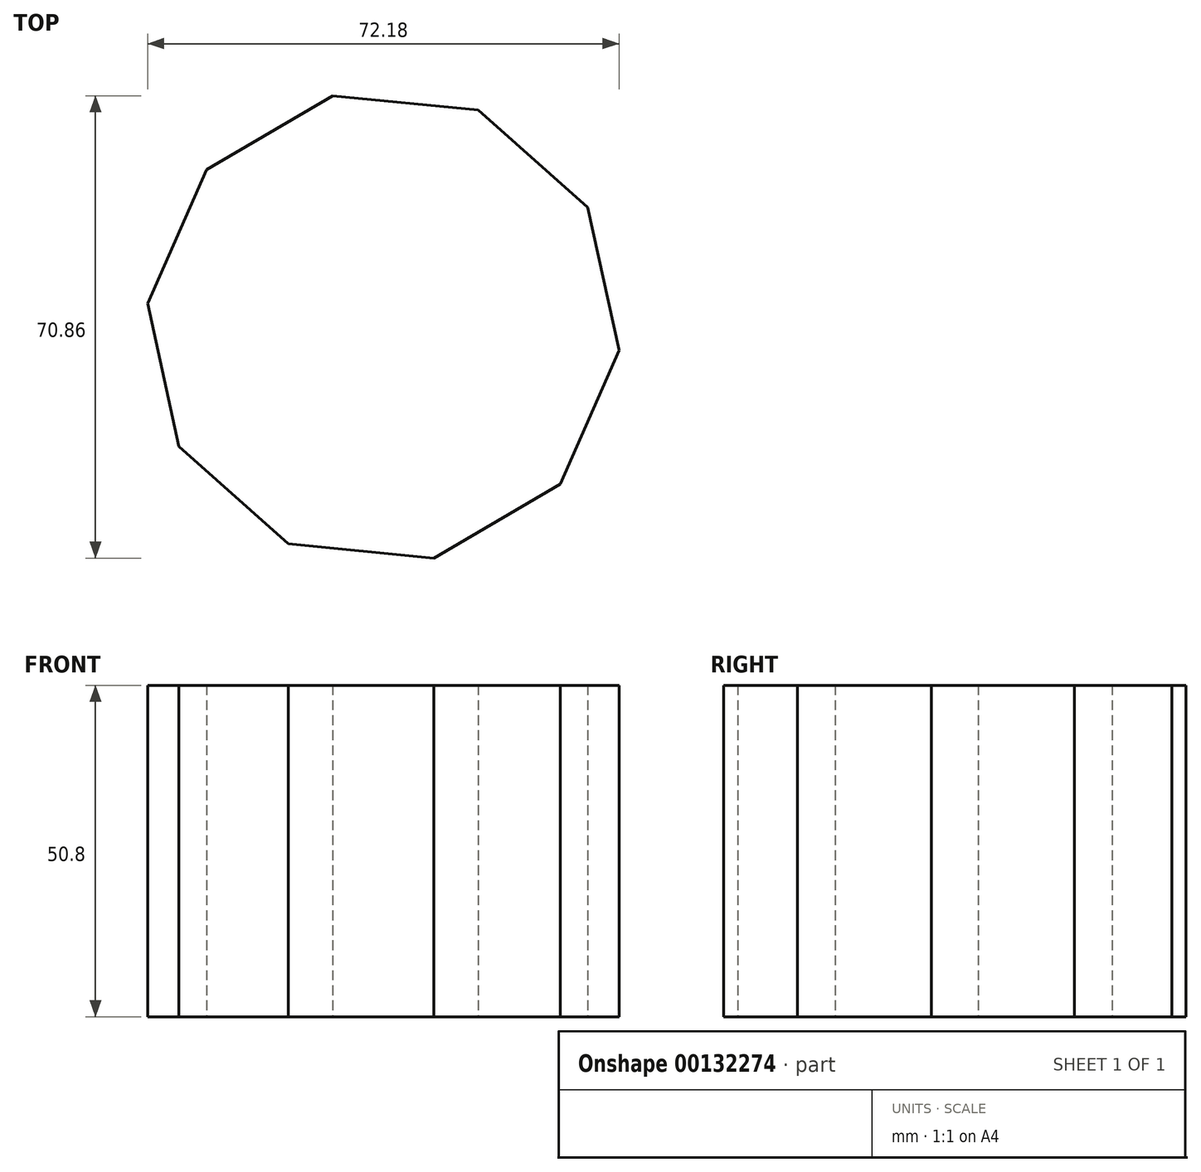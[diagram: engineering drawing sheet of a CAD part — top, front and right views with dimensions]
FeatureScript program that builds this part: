
annotation { "Feature Type Name" : "Feature", "Feature Type Description" : "" }
export const myFeature = defineFeature(function(context is Context, id is Id, definition is map)
    precondition{}
    {
        {
            var Q0;
            Q0=qCreatedBy(makeId("Top.planeOp"),FACE);
            var sketch = newSketch(context, id + "F0", { "sketchPlane" : qUnion([Q0])});
            skCircle(sketch, "E0.cCircle", {"center": v(0, 0) * mm, "radius": 34.5 * mm, "construction": true});
            skLineSegment(sketch, "E0.0", {"start": v(-27.1, 24.1) * mm, "end": v(-7.75, 35.43) * mm});
            skLineSegment(sketch, "E0.1", {"start": v(-7.75, 35.43) * mm, "end": v(14.55, 33.22) * mm});
            skLineSegment(sketch, "E0.2", {"start": v(14.55, 33.22) * mm, "end": v(31.3, 18.32) * mm});
            skLineSegment(sketch, "E0.3", {"start": v(31.3, 18.32) * mm, "end": v(36.1, -3.57) * mm});
            skLineSegment(sketch, "E0.4", {"start": v(36.1, -3.57) * mm, "end": v(27.1, -24.1) * mm});
            skLineSegment(sketch, "E0.5", {"start": v(27.1, -24.1) * mm, "end": v(7.75, -35.43) * mm});
            skLineSegment(sketch, "E0.6", {"start": v(7.75, -35.43) * mm, "end": v(-14.55, -33.22) * mm});
            skLineSegment(sketch, "E0.7", {"start": v(-14.55, -33.22) * mm, "end": v(-31.3, -18.32) * mm});
            skLineSegment(sketch, "E0.8", {"start": v(-31.3, -18.32) * mm, "end": v(-36.1, 3.57) * mm});
            skLineSegment(sketch, "E0.9", {"start": v(-36.1, 3.57) * mm, "end": v(-27.1, 24.1) * mm});
            skPoint(sketch, "E0.0.midPoint", {"position": v(-17.43, 29.77) * mm});
            skSolve(sketch);
        }
        {
            var Q0;
            Q0 = qSketchRegion(id + "F0", true);
            extrude(context, id + "F1", {"entities" : qUnion([Q0]), "depth" : 50.8 * mm});
        }
    });
